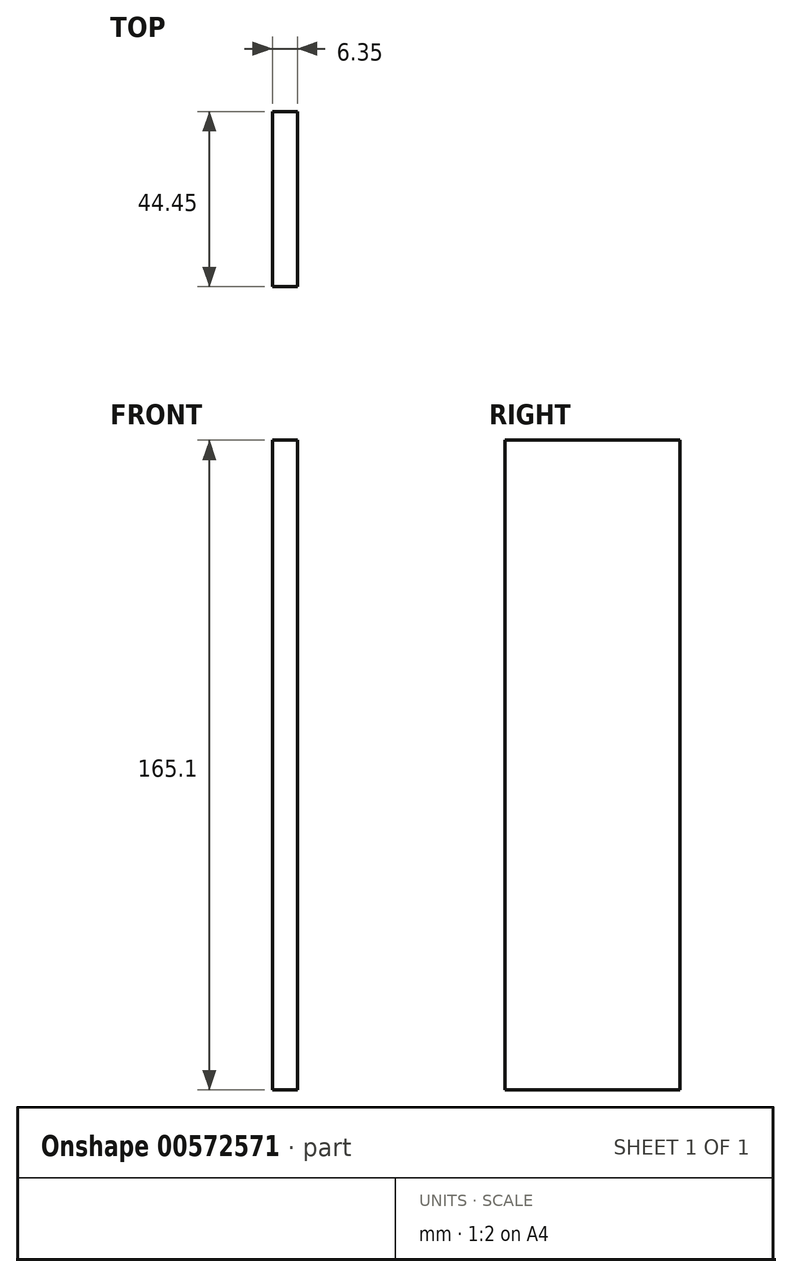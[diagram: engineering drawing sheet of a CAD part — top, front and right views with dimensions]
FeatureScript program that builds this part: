
annotation { "Feature Type Name" : "Feature", "Feature Type Description" : "" }
export const myFeature = defineFeature(function(context is Context, id is Id, definition is map)
    precondition{}
    {
        {
            var Q0;
            Q0=qCreatedBy(makeId("Right.planeOp"),FACE);
            var sketch = newSketch(context, id + "F0", { "sketchPlane" : qUnion([Q0])});
            skLineSegment(sketch, "E0.bottom", {"start": v(-94.16, 55.1) * mm, "end": v(-49.7, 55.1) * mm});
            skLineSegment(sketch, "E0.top", {"start": v(-94.16, -110) * mm, "end": v(-49.7, -110) * mm});
            skLineSegment(sketch, "E0.left", {"start": v(-94.16, 55.1) * mm, "end": v(-94.16, -110) * mm});
            skLineSegment(sketch, "E1", {"start": v(-49.7, -110) * mm, "end": v(-49.7, 55.1) * mm});
            skSolve(sketch);
        }
        {
            var Q0;
            Q0=makeQuery(id+"F0.imprint","IMPRINT",FACE,{"disambiguationData":[TD([[makeQuery(id+"F0.imprint","IMPRINT",EDGE,{"derivedFrom":sQuery(id+"F0.wireOp",EDGE,"E0.bottom")}),-1.0]])]});
            extrude(context, id + "F1", {"entities" : qUnion([Q0]), "depth" : 6.35 * mm, "offsetDistance" : 25.4 * mm});
        }
    });
